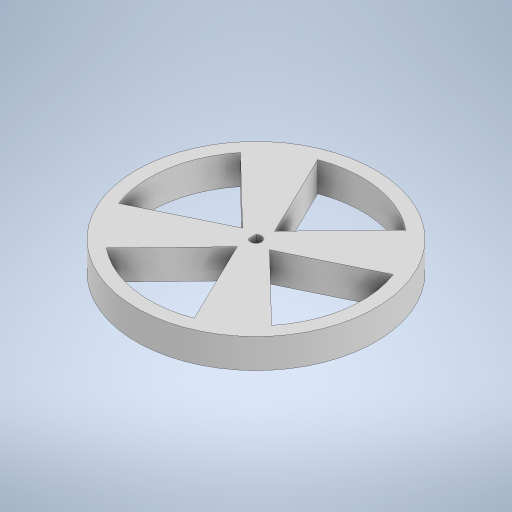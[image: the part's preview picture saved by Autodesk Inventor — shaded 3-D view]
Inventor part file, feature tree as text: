
AUTODESK INVENTOR PART (.ipt)
format: ipt  version: 2024.2 (Build 282272000, 272)  size: 267,264 bytes
history: native  units: mm
features: other x1, extrude x1, sketch x1
ambient origin geometry x8: Origin, YZ Plane, XZ Plane, XY Plane, X Axis, Y Axis, Z Axis, Center Point
bodies: Body1 (feature_tree)
feature tree (3):
  other  "Bryła1"
  extrude  "Wyciągnięcie proste1"  Depth=73.0mm
  sketch  "Szkic1"
